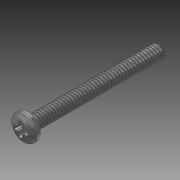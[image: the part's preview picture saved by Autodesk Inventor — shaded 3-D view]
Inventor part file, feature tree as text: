
AUTODESK INVENTOR PART (.ipt)
format: ipt  version: 2014 SP1 (Build 180222100, 222)  size: 1,099,264 bytes
history: native  units: in
note: dims shown in document units (in); Inventor stores cm internally (conversion verified against a paired STEP export)
features: fillet x1, other x1, imported_body x1
ambient origin geometry x8: Origin, YZ Plane, XZ Plane, XY Plane, X Axis, Y Axis, Z Axis, Center Point
bodies: Body1 (feature_tree)
feature tree (3):
  fillet  "Fillet1"  [1 undecoded]
  other  "91772A1181"
  imported_body  "Base1"
note: 1 required parameter value undecoded (feature->parameter linkage not recoverable at this tier; creation-order binding heuristic only, values carry confidence <= 0.55)
